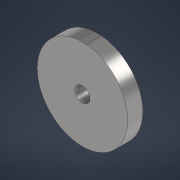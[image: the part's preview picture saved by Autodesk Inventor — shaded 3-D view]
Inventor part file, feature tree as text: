
AUTODESK INVENTOR PART (.ipt)
format: ipt  version: 2021 (Build 250183000, 183)  size: 109,568 bytes
history: native  units: mm
features: sketch x3, extrude x2, hole x1
ambient origin geometry x8: Origin, YZ Plane, XZ Plane, XY Plane, X Axis, Y Axis, Z Axis, Center Point
bodies: Solid1 (feature_tree)
feature tree (6):
  extrude  "Extrusion1"  Depth=10.0mm
  extrude  "Extrusion2"  Depth=10.0mm TaperAngle=0.0deg
  hole  "Hole1"  [1 undecoded]
  sketch  "Sketch1"  dims[d0=10.0mm d1=0.0mm d2=60.0mm]
  sketch  "Sketch2"  dims[d3=5.0mm d4=10.0mm d5=0.0mm]
  sketch  "Sketch3"  dims[d6=10.0mm d7=6.0mm d8=4.0mm d9=2.0mm d10=90.0deg d11=8.0mm d12=20.594885mm]
note: 1 required parameter value undecoded (feature->parameter linkage not recoverable at this tier; creation-order binding heuristic only, values carry confidence <= 0.55)
